# Revit family: Trane_TVR_Outdoor_4TVH0229(249_268_290_307)EE000AA_380~415V(50_60Hz)
name_source: partatom
category: Equipamento mecânico
units: mm (PartAtom-declared; Revit-internal decimal feet)

## family parameters
Com base no plano de trabalho = Não
Compartilhado = Não
Corte com vazios quando carregada = Não
Cota do conector redondo = Utilizar diâmetro
Número OmniClass = 23.75.00.00
Ponto de cálculo do ambiente = Não
Sempre na vertical = Sim
Tipo de parte = Normal
Título OmniClass = Climate Control (HVAC)

## types (5) — shared parameters
Casing color = White
Compressor = 2
Condensation = Air
Depth = 850
Descrição = High efficiency air cooled
Fabricante = Trane
Gas = R410A
Height = 1830  [stored 6.00394 ft]
Installation = Outdoor installation
Machine material = Galvanized Steel
Series = ULTRA
URL = https://www.trane.com
Width = 1730
clearance access behind = 1000  [stored 3.28084 ft]
clearance access front = 1000  [stored 3.28084 ft]
clearance access left = 1000  [stored 3.28084 ft]
clearance access right = 1000  [stored 3.28084 ft]

## per-type parameters (varying)
| type | Air Flow | Cooling Capacity | Cooling Power Input | Gas pipe | Heating Capacity | Heating Power Input | Liquid pipe | Maximum Fuse Amps | Minimum Circuit Amps | Net Weight | Power supply |
| 4TVH0229EE000AA | 25000.000 m³/h | 67.000 kW | 16.580 kW | 31.8 | 67.000 kW | 15.120 kW | 19.1 | 63 A | 48 A | 430.00 kg | 380V 3Ph~60Hz |
| 4TVH0249EE000AA | 25000.000 m³/h | 73.000 kW | 19.110 kW | 31.8 | 73.000 kW | 17.380 kW | 22.2 | 63 A | 53 A | 430.00 kg | 220V 3Ph~60Hz |
| 4TVH0268EE000AA | 25000.000 m³/h | 78.500 kW | 23.430 kW | 31.8 | 78.500 kW | 20.230 kW | 22.2 | 63 A | 59 A | 430.00 kg | 380V 3Ph~60Hz |
| 4TVH0290EE000AA | 24000.000 m³/h | 85.000 kW | 25.680 kW | 38.1  [stored 0.125 ft] | 85.000 kW | 22.550 kW | 22.2 | 80 A | 65 A | 475.00 kg | 380V 3Ph~60Hz |
| 4TVH0307EE000AA | 24000.000 m³/h | 90.000 kW | 25.280 kW | 38.1  [stored 0.125 ft] | 90.000 kW | 28.300 kW | 22.2 | 80 A | 67 A | 475.00 kg | 380V 3Ph~60Hz |

note: column(s) folded — value = type name in every type: Modelo

note: [stored X ft] marks values corroborated as IEEE doubles in the binary element streams (Revit-internal decimal feet)

## geometry (parser evidence)
native form markers: Blend x2, Sweep x18
no freeform markers — native parametric forms only
